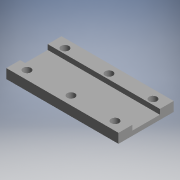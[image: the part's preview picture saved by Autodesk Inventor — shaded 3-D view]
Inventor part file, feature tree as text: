
AUTODESK INVENTOR PART (.ipt)
format: ipt  version: 2017.3 (Build 213256000, 256)  size: 125,952 bytes
history: native  units: mm (DEFAULTED — no unit token found)
features: other x49, sketch x3, extrude x2, hole x1, pattern_linear x1
ambient origin geometry x8: Origin, YZ Plane, XZ Plane, XY Plane, X Axis, Y Axis, Z Axis, Center Point
bodies: Solid1 (feature_tree)
feature tree (56):
  extrude  "Extrusion1"  Depth=5.5mm
  hole  "Hole1"  [1 undecoded]
  pattern_linear  "Rectangular Pattern1"  [2 undecoded]
  extrude  "Extrusion2"  [1 undecoded]
  other  "tbck_XY"
  other  "tbck_YZ"
  other  "tbck_ZX"
  other  "tbck_X"
  other  "tbck_Y"
  other  "tbck_Z"
  other  "tbck_Center"
  other  "tbck_hole_1_XY"
  other  "tbck_hole_1_YZ"
  other  "tbck_hole_1_ZX"
  other  "tbck_hole_1_X"
  other  "tbck_hole_1_Y"
  other  "tbck_hole_1_Z"
  other  "tbck_hole_1_Center"
  other  "tbck_hole_2_XY"
  other  "tbck_hole_2_YZ"
  other  "tbck_hole_2_ZX"
  other  "tbck_hole_2_X"
  other  "tbck_hole_2_Y"
  other  "tbck_hole_2_Z"
  other  "tbck_hole_2_Center"
  other  "tbck_hole_3_XY"
  other  "tbck_hole_3_YZ"
  other  "tbck_hole_3_ZX"
  other  "tbck_hole_3_X"
  other  "tbck_hole_3_Y"
  other  "tbck_hole_3_Z"
  other  "tbck_hole_3_Center"
  other  "tbck_holes_1_XY"
  other  "tbck_holes_1_YZ"
  other  "tbck_holes_1_ZX"
  other  "tbck_holes_1_X"
  other  "tbck_holes_1_Y"
  other  "tbck_holes_1_Z"
  other  "tbck_holes_1_Center"
  other  "tbck_holes_2_XY"
  other  "tbck_holes_2_YZ"
  other  "tbck_holes_2_ZX"
  other  "tbck_holes_2_X"
  other  "tbck_holes_2_Y"
  other  "tbck_holes_2_Z"
  other  "tbck_holes_2_Center"
  other  "tbck_holes_3_XY"
  other  "tbck_holes_3_YZ"
  other  "tbck_holes_3_ZX"
  other  "tbck_holes_3_X"
  other  "tbck_holes_3_Y"
  other  "tbck_holes_3_Z"
  other  "tbck_holes_3_Center"
  sketch  "Sketch_1"  dims[d0=5.5mm d1=0.0mm]
  sketch  "Sketch2"  dims[d2=4.5mm d3=6.0mm d4=4.0mm d5=2.0mm d6=90.0deg d7=5.5mm d8=0.0mm d9=30.0mm d11=25.5mm d12=20.0mm d14=22.0mm]
  sketch  "Sketch_4"  dims[d15=65.0mm d16=0.0mm d17=0.0mm d18=0.0mm d19=0.0mm d20=0.0mm d21=0.0mm d22=0.0mm]
note: 4 required parameter values undecoded (feature->parameter linkage not recoverable at this tier; creation-order binding heuristic only, values carry confidence <= 0.55)
